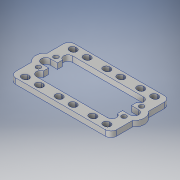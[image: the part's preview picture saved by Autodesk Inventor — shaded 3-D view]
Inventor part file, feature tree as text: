
AUTODESK INVENTOR PART (.ipt)
format: ipt  version: 2019 (Build 230136000, 136)  size: 179,200 bytes
history: native  units: in
note: dims shown in document units (in); Inventor stores cm internally (conversion verified against a paired STEP export)
features: mirror x1
ambient origin geometry x8: Origin, YZ Plane, XZ Plane, XY Plane, X Axis, Y Axis, Z Axis, Center Point
bodies: Solid1 (feature_tree)
feature tree (1):
  mirror  "Mirror2"
